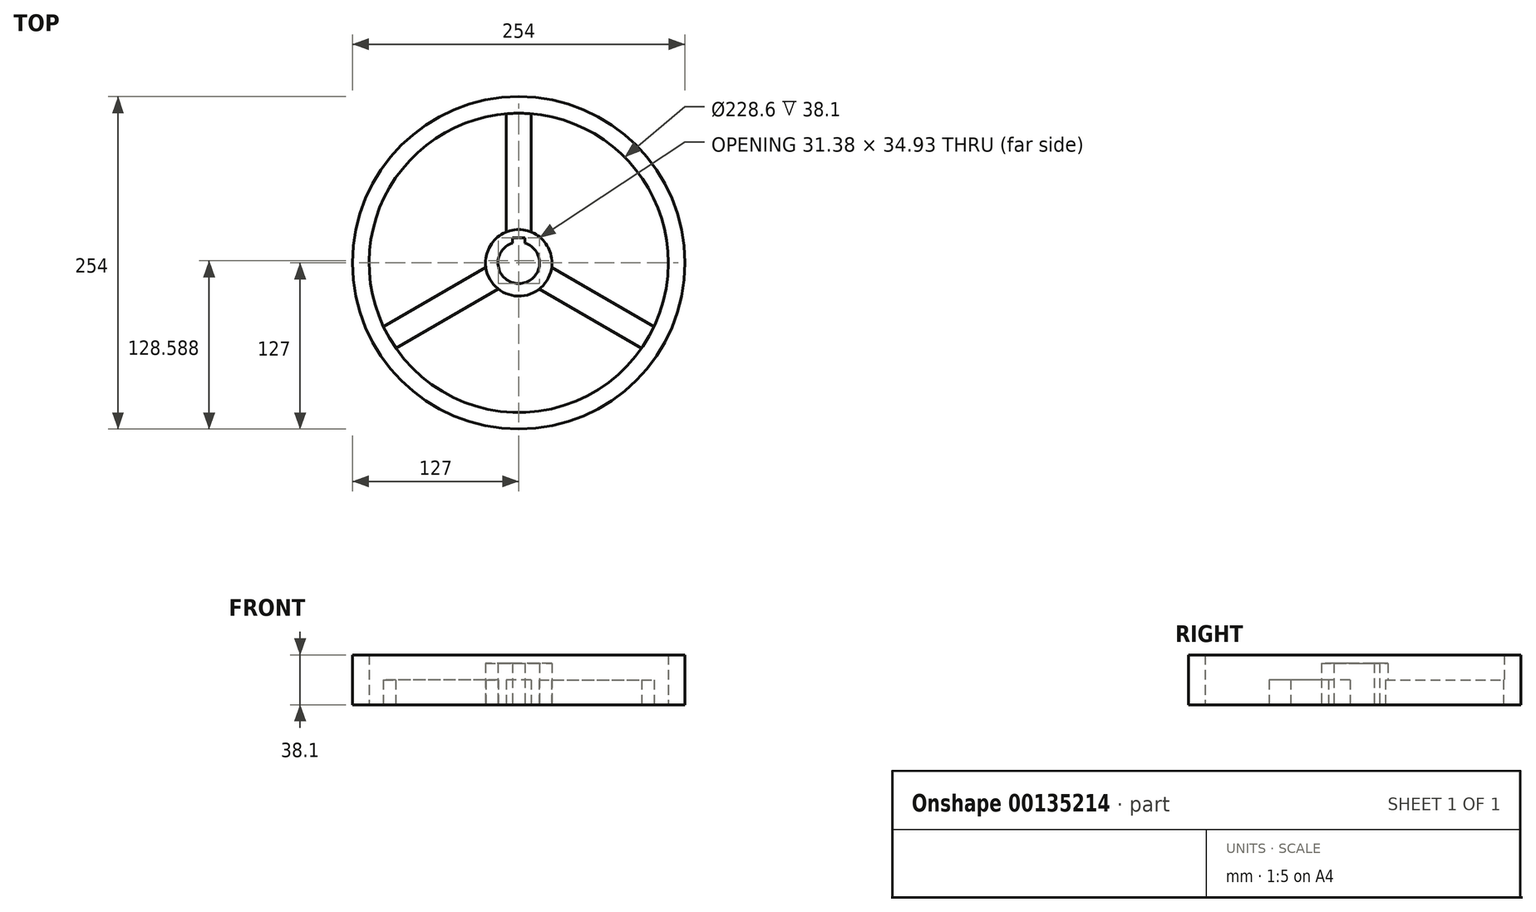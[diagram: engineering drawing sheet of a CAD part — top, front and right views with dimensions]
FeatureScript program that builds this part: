
annotation { "Feature Type Name" : "Feature", "Feature Type Description" : "" }
export const myFeature = defineFeature(function(context is Context, id is Id, definition is map)
    precondition{}
    {
        {
            var Q0;
            Q0=qCreatedBy(makeId("Top.planeOp"),FACE);
            var sketch = newSketch(context, id + "F0", { "sketchPlane" : qUnion([Q0])});
            skCircle(sketch, "E0", {"center": v(0, 0) * mm, "radius": 127 * mm});
            skCircle(sketch, "E1", {"center": v(0, 0) * mm, "radius": 114.3 * mm});
            skCircle(sketch, "E2", {"center": v(0, 0) * mm, "radius": 25.4 * mm});
            skCircle(sketch, "E3", {"center": v(0, 0) * mm, "radius": 15.88 * mm});
            skLineSegment(sketch, "E4", {"start": v(-9.52, 23.55) * mm, "end": v(-9.53, 113.9) * mm});
            skLineSegment(sketch, "E5", {"start": v(9.53, 23.55) * mm, "end": v(9.52, 113.9) * mm});
            skLineSegment(sketch, "E6", {"start": v(-25.15, -3.52) * mm, "end": v(-103.4, -48.7) * mm});
            skLineSegment(sketch, "E7", {"start": v(-15.63, -20.02) * mm, "end": v(-93.88, -65.2) * mm});
            skLineSegment(sketch, "E8", {"start": v(15.63, -20.02) * mm, "end": v(93.88, -65.2) * mm});
            skLineSegment(sketch, "E9", {"start": v(25.15, -3.52) * mm, "end": v(103.4, -48.7) * mm});
            skLineSegment(sketch, "E10", {"start": v(-4.77, 15.14) * mm, "end": v(-4.77, 19.05) * mm});
            skLineSegment(sketch, "E11", {"start": v(-4.77, 19.05) * mm, "end": v(4.76, 19.05) * mm});
            skLineSegment(sketch, "E12", {"start": v(4.76, 19.05) * mm, "end": v(4.76, 15.14) * mm});
            skSolve(sketch);
        }
        {
            var Q0;
            Q0=makeQuery(id+"F0.imprint","IMPRINT",FACE,{"disambiguationData":[TD([[makeQuery(id+"F0.imprint","IMPRINT",EDGE,{"derivedFrom":sQuery(id+"F0.wireOp",EDGE,"E0")}),1.0]])]});
            extrude(context, id + "F1", {"entities" : qUnion([Q0]), "depth" : 38.1 * mm});
        }
        {
            var Q0;
            {var subQ0=sQuery(id+"F0.wireOp",EDGE,"E4");Q0=makeQuery(id+"F0.imprint","IMPRINT",FACE,{"disambiguationData":[TD([[makeQuery(id+"F0.imprint","IMPRINT",EDGE,{"derivedFrom":subQ0}),-1.0]])]});}
            var Q1;
            {var subQ0=sQuery(id+"F0.wireOp",EDGE,"E6");Q1=makeQuery(id+"F0.imprint","IMPRINT",FACE,{"disambiguationData":[TD([[makeQuery(id+"F0.imprint","IMPRINT",EDGE,{"derivedFrom":subQ0}),1.0]])]});}
            var Q2;
            {var subQ0=sQuery(id+"F0.wireOp",EDGE,"E8");Q2=makeQuery(id+"F0.imprint","IMPRINT",FACE,{"disambiguationData":[TD([[makeQuery(id+"F0.imprint","IMPRINT",EDGE,{"derivedFrom":subQ0}),1.0]])]});}
            extrude(context, id + "F2", {"entities" : qUnion([Q0, Q1, Q2]), "operationType" : NewBodyOperationType.ADD, "depth" : 19.05 * mm});
        }
        {
            var Q0;
            {var subQ6=sQuery(id+"F0.wireOp",EDGE,"E10");Q0=makeQuery(id+"F0.imprint","IMPRINT",FACE,{"disambiguationData":[TD([[makeQuery(id+"F0.imprint","IMPRINT",EDGE,{"derivedFrom":subQ6}),1.0]])]});}
            extrude(context, id + "F3", {"entities" : qUnion([Q0]), "operationType" : NewBodyOperationType.ADD, "depth" : 31.75 * mm});
        }
    });
